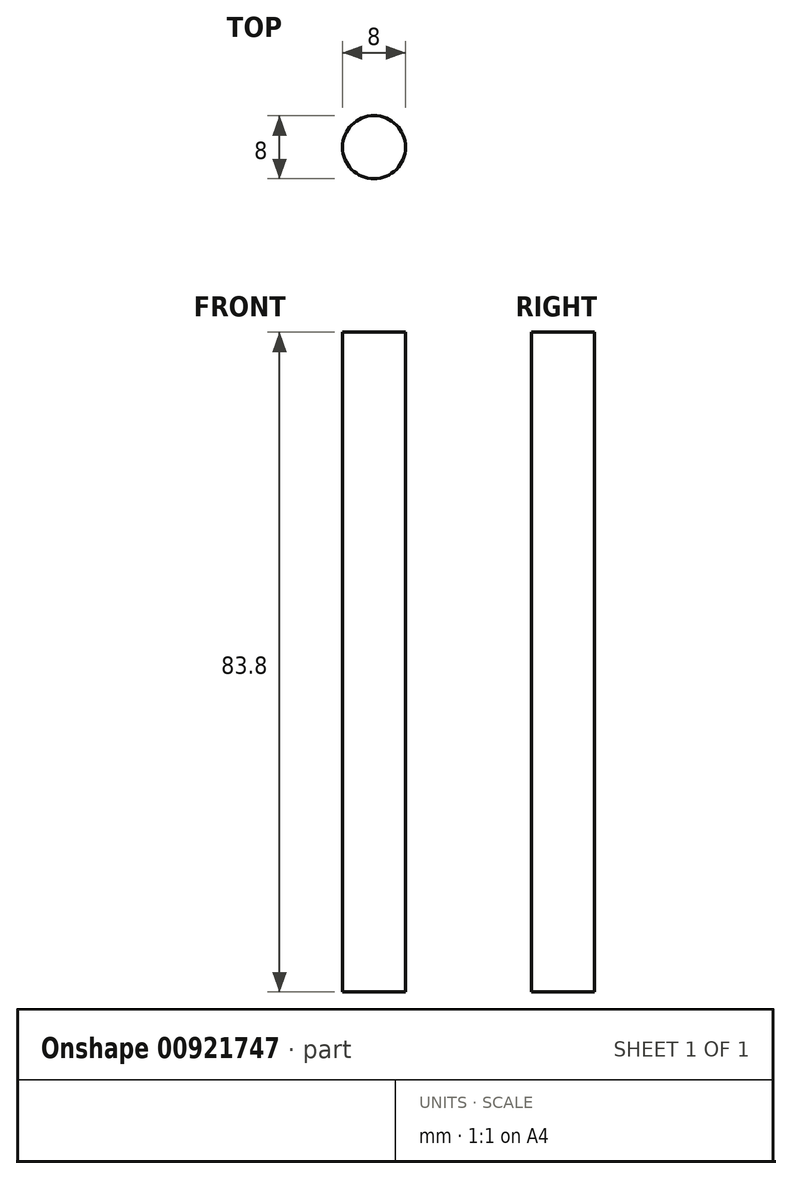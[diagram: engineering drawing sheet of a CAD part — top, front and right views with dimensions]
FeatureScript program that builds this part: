
annotation { "Feature Type Name" : "Feature", "Feature Type Description" : "" }
export const myFeature = defineFeature(function(context is Context, id is Id, definition is map)
    precondition{}
    {
        {
            var Q0;
            Q0=qCreatedBy(makeId("Top.planeOp"),FACE);
            var sketch = newSketch(context, id + "F0", { "sketchPlane" : qUnion([Q0])});
            skCircle(sketch, "E0", {"center": v(0, 0) * mm, "radius": 4 * mm});
            skSolve(sketch);
        }
        {
            var Q0;
            Q0=makeQuery(id+"F0.imprint","IMPRINT",FACE,{"disambiguationData":[TD([[makeQuery(id+"F0.imprint","IMPRINT",EDGE,{"derivedFrom":sQuery(id+"F0.wireOp",EDGE,"E0")}),1.0]])]});
            extrude(context, id + "F1", {"entities" : qUnion([Q0]), "depth" : 83.8 * mm, "offsetDistance" : 25 * mm});
        }
    });
